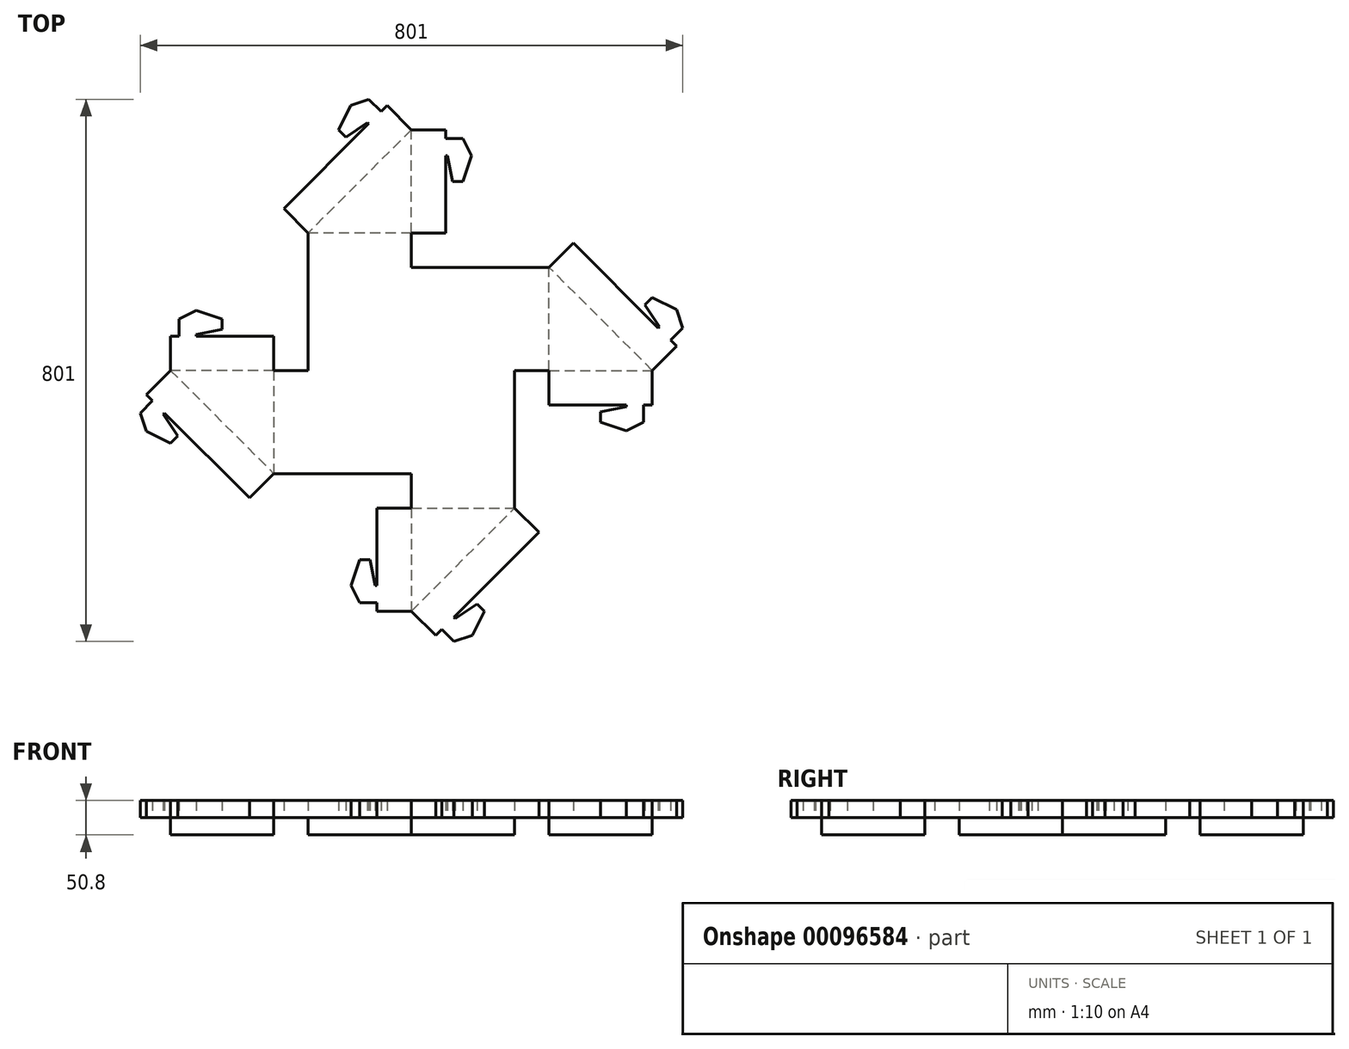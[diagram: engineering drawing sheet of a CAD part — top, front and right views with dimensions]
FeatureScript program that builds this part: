
annotation { "Feature Type Name" : "Feature", "Feature Type Description" : "" }
export const myFeature = defineFeature(function(context is Context, id is Id, definition is map)
    precondition{}
    {
        {
            var Q0;
            Q0=qCreatedBy(makeId("Top.planeOp"),FACE);
            var sketch = newSketch(context, id + "F0", { "sketchPlane" : qUnion([Q0])});
            skLineSegment(sketch, "E0.bottom", {"start": v(0, 0) * mm, "end": v(-152.4, 0) * mm});
            skLineSegment(sketch, "E0.top", {"start": v(0, 152.4) * mm, "end": v(-152.4, 152.4) * mm});
            skLineSegment(sketch, "E0.left", {"start": v(0, 0) * mm, "end": v(0, 152.4) * mm});
            skLineSegment(sketch, "E0.right", {"start": v(-152.4, 0) * mm, "end": v(-152.4, 152.4) * mm});
            skLineSegment(sketch, "E1.top", {"start": v(0, 203.2) * mm, "end": v(-152.4, 203.2) * mm});
            skLineSegment(sketch, "E1.left", {"start": v(0, 152.4) * mm, "end": v(0, 203.2) * mm});
            skLineSegment(sketch, "E1.right", {"start": v(-152.4, 152.4) * mm, "end": v(-152.4, 203.2) * mm});
            skLineSegment(sketch, "E2", {"start": v(0, 203.2) * mm, "end": v(0, 355.6) * mm});
            skLineSegment(sketch, "E3", {"start": v(0, 355.6) * mm, "end": v(-152.4, 203.2) * mm});
            skLineSegment(sketch, "E4", {"start": v(0, 355.6) * mm, "end": v(50.8, 355.6) * mm});
            skLineSegment(sketch, "E5", {"start": v(50.8, 355.6) * mm, "end": v(50.8, 203.2) * mm});
            skLineSegment(sketch, "E6", {"start": v(50.8, 203.2) * mm, "end": v(0, 203.2) * mm});
            skLineSegment(sketch, "E7", {"start": v(0, 355.6) * mm, "end": v(-35.92, 391.52) * mm});
            skLineSegment(sketch, "E8", {"start": v(-35.92, 391.52) * mm, "end": v(-188.32, 239.12) * mm});
            skLineSegment(sketch, "E9", {"start": v(-188.32, 239.12) * mm, "end": v(-152.4, 203.2) * mm});
            skLineSegment(sketch, "E10", {"start": v(50.8, 317.5) * mm, "end": v(53.34, 317.5) * mm});
            skLineSegment(sketch, "E11", {"start": v(53.34, 317.5) * mm, "end": v(60.96, 279.4) * mm});
            skLineSegment(sketch, "E12", {"start": v(60.96, 279.4) * mm, "end": v(76.2, 279.4) * mm});
            skLineSegment(sketch, "E13", {"start": v(76.2, 279.4) * mm, "end": v(88.9, 317.5) * mm});
            skLineSegment(sketch, "E14", {"start": v(88.9, 317.5) * mm, "end": v(76.2, 342.9) * mm});
            skLineSegment(sketch, "E15", {"start": v(76.2, 342.9) * mm, "end": v(50.8, 342.9) * mm});
            skLineSegment(sketch, "E16", {"start": v(50.8, 342.9) * mm, "end": v(50.8, 317.5) * mm});
            skLineSegment(sketch, "E17", {"start": v(88.9, 353.3) * mm, "end": v(88.9, 210.85) * mm});
            skLineSegment(sketch, "E18", {"start": v(-44.9, 382.54) * mm, "end": v(-62.86, 400.5) * mm});
            skLineSegment(sketch, "E19", {"start": v(-62.86, 400.5) * mm, "end": v(-89.8, 391.52) * mm});
            skLineSegment(sketch, "E20", {"start": v(-89.8, 391.52) * mm, "end": v(-107.76, 355.6) * mm});
            skLineSegment(sketch, "E21", {"start": v(-107.76, 355.6) * mm, "end": v(-96.99, 344.82) * mm});
            skLineSegment(sketch, "E22", {"start": v(-96.99, 344.82) * mm, "end": v(-64.66, 366.38) * mm});
            skLineSegment(sketch, "E23", {"start": v(-64.66, 366.38) * mm, "end": v(-62.86, 364.58) * mm});
            skLineSegment(sketch, "E24", {"start": v(-185.76, 295.57) * mm, "end": v(-62.64, 418.68) * mm});
            skLineSegment(sketch, "E25", {"start": v(-64.66, 366.38) * mm, "end": v(-89.8, 391.52) * mm});
            skLineSegment(sketch, "E26.1.0", {"start": v(-295.57, -185.76) * mm, "end": v(-418.68, -62.64) * mm});
            skLineSegment(sketch, "E26.1.1", {"start": v(-355.6, 50.8) * mm, "end": v(-203.2, 50.8) * mm});
            skLineSegment(sketch, "E26.1.2", {"start": v(-355.6, 0) * mm, "end": v(-355.6, 50.8) * mm});
            skLineSegment(sketch, "E26.1.3", {"start": v(0, 0) * mm, "end": v(0, -152.4) * mm});
            skLineSegment(sketch, "E26.1.4", {"start": v(-355.6, 0) * mm, "end": v(-203.2, -152.4) * mm});
            skLineSegment(sketch, "E26.1.5", {"start": v(-203.2, 50.8) * mm, "end": v(-203.2, 0) * mm});
            skLineSegment(sketch, "E26.1.6", {"start": v(-400.5, -62.86) * mm, "end": v(-391.52, -89.8) * mm});
            skLineSegment(sketch, "E26.1.7", {"start": v(-239.12, -188.32) * mm, "end": v(-203.2, -152.4) * mm});
            skLineSegment(sketch, "E26.1.8", {"start": v(-203.2, 0) * mm, "end": v(-355.6, 0) * mm});
            skLineSegment(sketch, "E26.1.10", {"start": v(-317.5, 53.34) * mm, "end": v(-279.4, 60.96) * mm});
            skLineSegment(sketch, "E26.1.11", {"start": v(-382.54, -44.9) * mm, "end": v(-400.5, -62.86) * mm});
            skLineSegment(sketch, "E26.1.12", {"start": v(-342.9, 76.2) * mm, "end": v(-342.9, 50.8) * mm});
            skLineSegment(sketch, "E26.1.13", {"start": v(-391.52, -35.92) * mm, "end": v(-239.12, -188.32) * mm});
            skLineSegment(sketch, "E26.1.14", {"start": v(-279.4, 76.2) * mm, "end": v(-317.5, 88.9) * mm});
            skLineSegment(sketch, "E26.1.15", {"start": v(0, -152.4) * mm, "end": v(-152.4, -152.4) * mm});
            skLineSegment(sketch, "E26.1.16", {"start": v(-353.3, 88.9) * mm, "end": v(-210.85, 88.9) * mm});
            skLineSegment(sketch, "E26.1.17", {"start": v(-152.4, -152.4) * mm, "end": v(-203.2, -152.4) * mm});
            skLineSegment(sketch, "E26.1.18", {"start": v(-342.9, 50.8) * mm, "end": v(-317.5, 50.8) * mm});
            skLineSegment(sketch, "E26.1.19", {"start": v(-152.4, 0) * mm, "end": v(-203.2, 0) * mm});
            skLineSegment(sketch, "E26.1.20", {"start": v(-317.5, 88.9) * mm, "end": v(-342.9, 76.2) * mm});
            skLineSegment(sketch, "E26.1.21", {"start": v(-152.4, 0) * mm, "end": v(-152.4, -152.4) * mm});
            skLineSegment(sketch, "E26.1.22", {"start": v(-344.82, -96.99) * mm, "end": v(-366.38, -64.66) * mm});
            skLineSegment(sketch, "E26.1.23", {"start": v(-391.52, -89.8) * mm, "end": v(-355.6, -107.76) * mm});
            skLineSegment(sketch, "E26.1.24", {"start": v(-203.2, 0) * mm, "end": v(-203.2, -152.4) * mm});
            skLineSegment(sketch, "E26.1.25", {"start": v(-152.4, 0) * mm, "end": v(-152.4, -152.4) * mm});
            skLineSegment(sketch, "E26.1.26", {"start": v(-355.6, 0) * mm, "end": v(-391.52, -35.92) * mm});
            skLineSegment(sketch, "E26.1.27", {"start": v(-366.38, -64.66) * mm, "end": v(-391.52, -89.8) * mm});
            skLineSegment(sketch, "E26.1.28", {"start": v(-279.4, 60.96) * mm, "end": v(-279.4, 76.2) * mm});
            skLineSegment(sketch, "E26.1.29", {"start": v(-355.6, -107.76) * mm, "end": v(-344.82, -96.99) * mm});
            skLineSegment(sketch, "E26.1.30", {"start": v(-317.5, 50.8) * mm, "end": v(-317.5, 53.34) * mm});
            skLineSegment(sketch, "E26.1.31", {"start": v(-366.38, -64.66) * mm, "end": v(-364.58, -62.86) * mm});
            skLineSegment(sketch, "E26.2.0", {"start": v(185.76, -295.57) * mm, "end": v(62.64, -418.68) * mm});
            skLineSegment(sketch, "E26.2.1", {"start": v(-50.8, -355.6) * mm, "end": v(-50.8, -203.2) * mm});
            skLineSegment(sketch, "E26.2.2", {"start": v(0, -355.6) * mm, "end": v(-50.8, -355.6) * mm});
            skLineSegment(sketch, "E26.2.3", {"start": v(0, 0) * mm, "end": v(152.4, 0) * mm});
            skLineSegment(sketch, "E26.2.4", {"start": v(0, -355.6) * mm, "end": v(152.4, -203.2) * mm});
            skLineSegment(sketch, "E26.2.5", {"start": v(-50.8, -203.2) * mm, "end": v(0, -203.2) * mm});
            skLineSegment(sketch, "E26.2.6", {"start": v(62.86, -400.5) * mm, "end": v(89.8, -391.52) * mm});
            skLineSegment(sketch, "E26.2.7", {"start": v(188.32, -239.12) * mm, "end": v(152.4, -203.2) * mm});
            skLineSegment(sketch, "E26.2.8", {"start": v(0, -203.2) * mm, "end": v(0, -355.6) * mm});
            skLineSegment(sketch, "E26.2.9", {"start": v(0, 0) * mm, "end": v(0, -152.4) * mm});
            skLineSegment(sketch, "E26.2.10", {"start": v(-53.34, -317.5) * mm, "end": v(-60.96, -279.4) * mm});
            skLineSegment(sketch, "E26.2.11", {"start": v(44.9, -382.54) * mm, "end": v(62.86, -400.5) * mm});
            skLineSegment(sketch, "E26.2.12", {"start": v(-76.2, -342.9) * mm, "end": v(-50.8, -342.9) * mm});
            skLineSegment(sketch, "E26.2.13", {"start": v(35.92, -391.52) * mm, "end": v(188.32, -239.12) * mm});
            skLineSegment(sketch, "E26.2.14", {"start": v(-76.2, -279.4) * mm, "end": v(-88.9, -317.5) * mm});
            skLineSegment(sketch, "E26.2.15", {"start": v(152.4, 0) * mm, "end": v(152.4, -152.4) * mm});
            skLineSegment(sketch, "E26.2.16", {"start": v(-88.9, -353.3) * mm, "end": v(-88.9, -210.85) * mm});
            skLineSegment(sketch, "E26.2.17", {"start": v(152.4, -152.4) * mm, "end": v(152.4, -203.2) * mm});
            skLineSegment(sketch, "E26.2.18", {"start": v(-50.8, -342.9) * mm, "end": v(-50.8, -317.5) * mm});
            skLineSegment(sketch, "E26.2.19", {"start": v(0, -152.4) * mm, "end": v(0, -203.2) * mm});
            skLineSegment(sketch, "E26.2.20", {"start": v(-88.9, -317.5) * mm, "end": v(-76.2, -342.9) * mm});
            skLineSegment(sketch, "E26.2.21", {"start": v(0, -152.4) * mm, "end": v(152.4, -152.4) * mm});
            skLineSegment(sketch, "E26.2.22", {"start": v(96.99, -344.82) * mm, "end": v(64.66, -366.38) * mm});
            skLineSegment(sketch, "E26.2.23", {"start": v(89.8, -391.52) * mm, "end": v(107.76, -355.6) * mm});
            skLineSegment(sketch, "E26.2.24", {"start": v(0, -203.2) * mm, "end": v(152.4, -203.2) * mm});
            skLineSegment(sketch, "E26.2.25", {"start": v(0, -152.4) * mm, "end": v(152.4, -152.4) * mm});
            skLineSegment(sketch, "E26.2.26", {"start": v(0, -355.6) * mm, "end": v(35.92, -391.52) * mm});
            skLineSegment(sketch, "E26.2.27", {"start": v(64.66, -366.38) * mm, "end": v(89.8, -391.52) * mm});
            skLineSegment(sketch, "E26.2.28", {"start": v(-60.96, -279.4) * mm, "end": v(-76.2, -279.4) * mm});
            skLineSegment(sketch, "E26.2.29", {"start": v(107.76, -355.6) * mm, "end": v(96.99, -344.82) * mm});
            skLineSegment(sketch, "E26.2.30", {"start": v(-50.8, -317.5) * mm, "end": v(-53.34, -317.5) * mm});
            skLineSegment(sketch, "E26.2.31", {"start": v(64.66, -366.38) * mm, "end": v(62.86, -364.58) * mm});
            skLineSegment(sketch, "E26.3.0", {"start": v(295.57, 185.76) * mm, "end": v(418.68, 62.64) * mm});
            skLineSegment(sketch, "E26.3.1", {"start": v(355.6, -50.8) * mm, "end": v(203.2, -50.8) * mm});
            skLineSegment(sketch, "E26.3.2", {"start": v(355.6, 0) * mm, "end": v(355.6, -50.8) * mm});
            skLineSegment(sketch, "E26.3.4", {"start": v(355.6, 0) * mm, "end": v(203.2, 152.4) * mm});
            skLineSegment(sketch, "E26.3.5", {"start": v(203.2, -50.8) * mm, "end": v(203.2, 0) * mm});
            skLineSegment(sketch, "E26.3.6", {"start": v(400.5, 62.86) * mm, "end": v(391.52, 89.8) * mm});
            skLineSegment(sketch, "E26.3.7", {"start": v(239.12, 188.32) * mm, "end": v(203.2, 152.4) * mm});
            skLineSegment(sketch, "E26.3.8", {"start": v(203.2, 0) * mm, "end": v(355.6, 0) * mm});
            skLineSegment(sketch, "E26.3.9", {"start": v(0, 0) * mm, "end": v(152.4, 0) * mm});
            skLineSegment(sketch, "E26.3.10", {"start": v(317.5, -53.34) * mm, "end": v(279.4, -60.96) * mm});
            skLineSegment(sketch, "E26.3.11", {"start": v(382.54, 44.9) * mm, "end": v(400.5, 62.86) * mm});
            skLineSegment(sketch, "E26.3.12", {"start": v(342.9, -76.2) * mm, "end": v(342.9, -50.8) * mm});
            skLineSegment(sketch, "E26.3.13", {"start": v(391.52, 35.92) * mm, "end": v(239.12, 188.32) * mm});
            skLineSegment(sketch, "E26.3.14", {"start": v(279.4, -76.2) * mm, "end": v(317.5, -88.9) * mm});
            skLineSegment(sketch, "E26.3.15", {"start": v(0, 152.4) * mm, "end": v(152.4, 152.4) * mm});
            skLineSegment(sketch, "E26.3.16", {"start": v(353.3, -88.9) * mm, "end": v(210.85, -88.9) * mm});
            skLineSegment(sketch, "E26.3.17", {"start": v(152.4, 152.4) * mm, "end": v(203.2, 152.4) * mm});
            skLineSegment(sketch, "E26.3.18", {"start": v(342.9, -50.8) * mm, "end": v(317.5, -50.8) * mm});
            skLineSegment(sketch, "E26.3.19", {"start": v(152.4, 0) * mm, "end": v(203.2, 0) * mm});
            skLineSegment(sketch, "E26.3.20", {"start": v(317.5, -88.9) * mm, "end": v(342.9, -76.2) * mm});
            skLineSegment(sketch, "E26.3.21", {"start": v(152.4, 0) * mm, "end": v(152.4, 152.4) * mm});
            skLineSegment(sketch, "E26.3.22", {"start": v(344.82, 96.99) * mm, "end": v(366.38, 64.66) * mm});
            skLineSegment(sketch, "E26.3.23", {"start": v(391.52, 89.8) * mm, "end": v(355.6, 107.76) * mm});
            skLineSegment(sketch, "E26.3.24", {"start": v(203.2, 0) * mm, "end": v(203.2, 152.4) * mm});
            skLineSegment(sketch, "E26.3.25", {"start": v(152.4, 0) * mm, "end": v(152.4, 152.4) * mm});
            skLineSegment(sketch, "E26.3.26", {"start": v(355.6, 0) * mm, "end": v(391.52, 35.92) * mm});
            skLineSegment(sketch, "E26.3.27", {"start": v(366.38, 64.66) * mm, "end": v(391.52, 89.8) * mm});
            skLineSegment(sketch, "E26.3.28", {"start": v(279.4, -60.96) * mm, "end": v(279.4, -76.2) * mm});
            skLineSegment(sketch, "E26.3.29", {"start": v(355.6, 107.76) * mm, "end": v(344.82, 96.99) * mm});
            skLineSegment(sketch, "E26.3.30", {"start": v(317.5, -50.8) * mm, "end": v(317.5, -53.34) * mm});
            skLineSegment(sketch, "E26.3.31", {"start": v(366.38, 64.66) * mm, "end": v(364.58, 62.86) * mm});
            skPoint(sketch, "E26.center", {"position": v(0, 0) * mm});
            skLineSegment(sketch, "E27", {"start": v(0, 152.4) * mm, "end": v(203.2, 152.4) * mm});
            skLineSegment(sketch, "E28", {"start": v(239.12, 188.32) * mm, "end": v(364.58, 62.86) * mm});
            skLineSegment(sketch, "E29", {"start": v(366.38, 64.66) * mm, "end": v(344.82, 96.99) * mm});
            skLineSegment(sketch, "E30", {"start": v(355.6, 107.76) * mm, "end": v(391.52, 89.8) * mm});
            skLineSegment(sketch, "E31", {"start": v(400.5, 62.86) * mm, "end": v(382.54, 44.9) * mm});
            skLineSegment(sketch, "E32", {"start": v(391.52, 35.92) * mm, "end": v(355.6, 0) * mm});
            skLineSegment(sketch, "E33", {"start": v(355.6, -50.8) * mm, "end": v(342.9, -50.8) * mm});
            skLineSegment(sketch, "E34", {"start": v(342.9, -76.2) * mm, "end": v(317.5, -88.9) * mm});
            skLineSegment(sketch, "E35", {"start": v(279.4, -76.2) * mm, "end": v(279.4, -60.96) * mm});
            skLineSegment(sketch, "E36", {"start": v(317.5, -53.34) * mm, "end": v(317.5, -50.8) * mm});
            skLineSegment(sketch, "E37", {"start": v(152.4, 0) * mm, "end": v(152.4, -203.2) * mm});
            skLineSegment(sketch, "E38", {"start": v(188.32, -239.12) * mm, "end": v(62.86, -364.58) * mm});
            skLineSegment(sketch, "E39", {"start": v(64.66, -366.38) * mm, "end": v(96.99, -344.82) * mm});
            skLineSegment(sketch, "E40", {"start": v(107.76, -355.6) * mm, "end": v(89.8, -391.52) * mm});
            skLineSegment(sketch, "E41", {"start": v(62.86, -400.5) * mm, "end": v(44.9, -382.54) * mm});
            skLineSegment(sketch, "E42", {"start": v(35.92, -391.52) * mm, "end": v(0, -355.6) * mm});
            skLineSegment(sketch, "E43", {"start": v(-50.8, -355.6) * mm, "end": v(-50.8, -342.9) * mm});
            skLineSegment(sketch, "E44", {"start": v(-76.2, -342.9) * mm, "end": v(-88.9, -317.5) * mm});
            skLineSegment(sketch, "E45", {"start": v(-76.2, -279.4) * mm, "end": v(-60.96, -279.4) * mm});
            skLineSegment(sketch, "E46", {"start": v(0, -152.4) * mm, "end": v(-203.2, -152.4) * mm});
            skLineSegment(sketch, "E47", {"start": v(-239.12, -188.32) * mm, "end": v(-364.58, -62.86) * mm});
            skLineSegment(sketch, "E48", {"start": v(-366.38, -64.66) * mm, "end": v(-344.82, -96.99) * mm});
            skLineSegment(sketch, "E49", {"start": v(-355.6, -107.76) * mm, "end": v(-391.52, -89.8) * mm});
            skLineSegment(sketch, "E50", {"start": v(-400.5, -62.86) * mm, "end": v(-382.54, -44.9) * mm});
            skLineSegment(sketch, "E51", {"start": v(-391.52, -35.92) * mm, "end": v(-355.6, 0) * mm});
            skLineSegment(sketch, "E52", {"start": v(-355.6, 50.8) * mm, "end": v(-342.9, 50.8) * mm});
            skSolve(sketch);
        }
        {
            var Q0;
            Q0 = qSketchRegion(id + "F0", true);
            extrude(context, id + "F1", {"entities" : qUnion([Q0]), "depth" : 25.4 * mm});
        }
        {
            var Q0;
            Q0=makeQuery(id+"F0.imprint","IMPRINT",FACE,{"disambiguationData":[TD([[makeQuery(id+"F0.imprint","IMPRINT",EDGE,{"derivedFrom":sQuery(id+"F0.wireOp",EDGE,"E26.3.4")}),1.0]])]});
            var Q1;
            Q1=makeQuery(id+"F0.imprint","IMPRINT",FACE,{"disambiguationData":[TD([[makeQuery(id+"F0.imprint","IMPRINT",EDGE,{"derivedFrom":sQuery(id+"F0.wireOp",EDGE,"E1.top")}),-1.0]])]});
            var Q2;
            Q2=makeQuery(id+"F0.imprint","IMPRINT",FACE,{"disambiguationData":[TD([[makeQuery(id+"F0.imprint","IMPRINT",EDGE,{"derivedFrom":sQuery(id+"F0.wireOp",EDGE,"E26.1.4")}),1.0]])]});
            var Q3;
            Q3=makeQuery(id+"F0.imprint","IMPRINT",FACE,{"disambiguationData":[TD([[makeQuery(id+"F0.imprint","IMPRINT",EDGE,{"derivedFrom":sQuery(id+"F0.wireOp",EDGE,"E26.2.4")}),1.0]])]});
            extrude(context, id + "F2", {"entities" : qUnion([Q0, Q1, Q2, Q3]), "operationType" : NewBodyOperationType.ADD, "oppositeDirection" : true, "depth" : 25.4 * mm});
        }
    });
